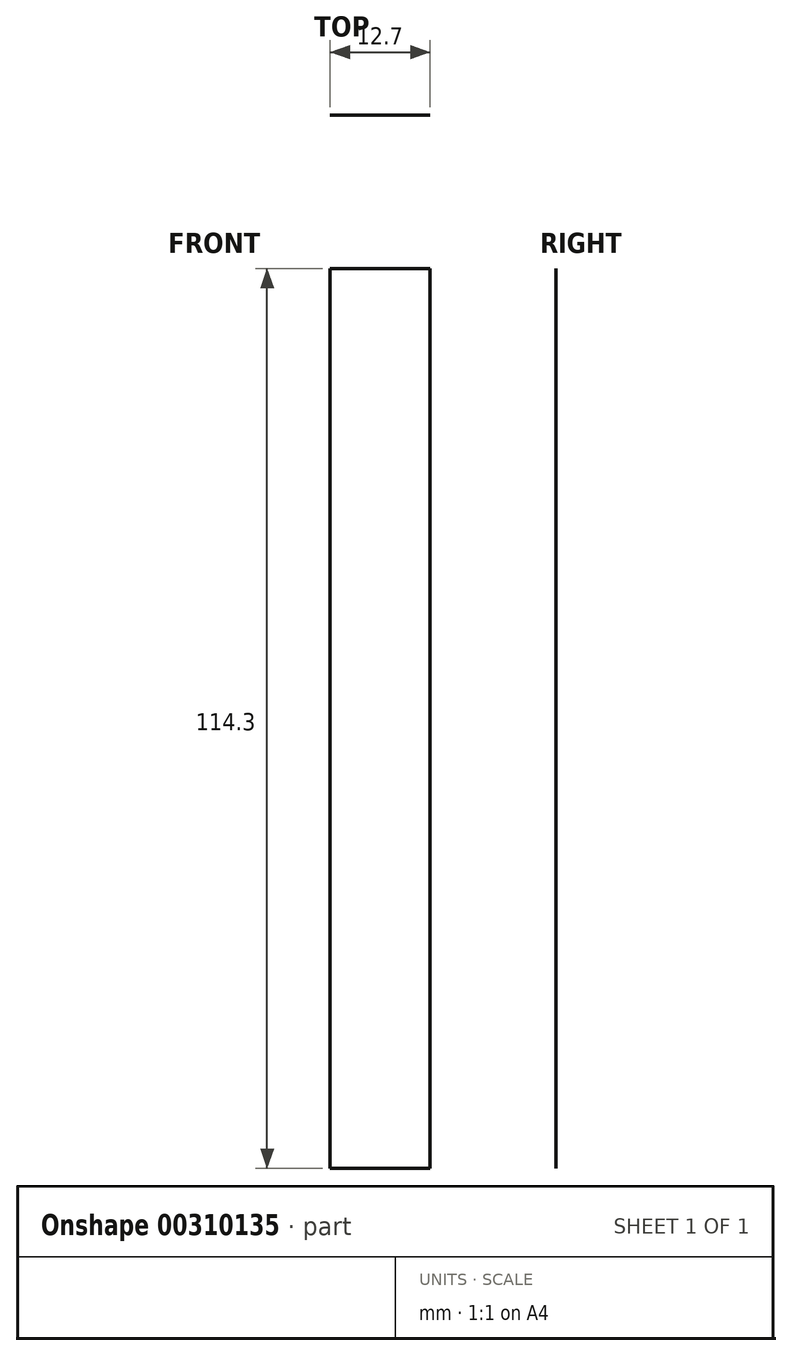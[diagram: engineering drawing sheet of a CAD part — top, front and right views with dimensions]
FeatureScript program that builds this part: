
annotation { "Feature Type Name" : "Feature", "Feature Type Description" : "" }
export const myFeature = defineFeature(function(context is Context, id is Id, definition is map)
    precondition{}
    {
        {
            var Q0;
            Q0=qCreatedBy(makeId("Front.planeOp"),FACE);
            var sketch = newSketch(context, id + "F0", { "sketchPlane" : qUnion([Q0])});
            skLineSegment(sketch, "E0.bottom", {"start": v(0, 0) * mm, "end": v(12.7, 0) * mm});
            skLineSegment(sketch, "E0.top", {"start": v(0, -114.3) * mm, "end": v(12.7, -114.3) * mm});
            skLineSegment(sketch, "E0.left", {"start": v(0, 0) * mm, "end": v(0, -114.3) * mm});
            skLineSegment(sketch, "E0.right", {"start": v(12.7, 0) * mm, "end": v(12.7, -114.3) * mm});
            skSolve(sketch);
        }
        {
            var Q0;
            Q0=makeQuery(id+"F0.imprint","IMPRINT",FACE,{"disambiguationData":[TD([[makeQuery(id+"F0.imprint","IMPRINT",EDGE,{"derivedFrom":sQuery(id+"F0.wireOp",EDGE,"E0.bottom")}),-1.0]])]});
            extrude(context, id + "F1", {"entities" : qUnion([Q0]), "depth" : 1 / 203.2 * mm});
        }
    });
